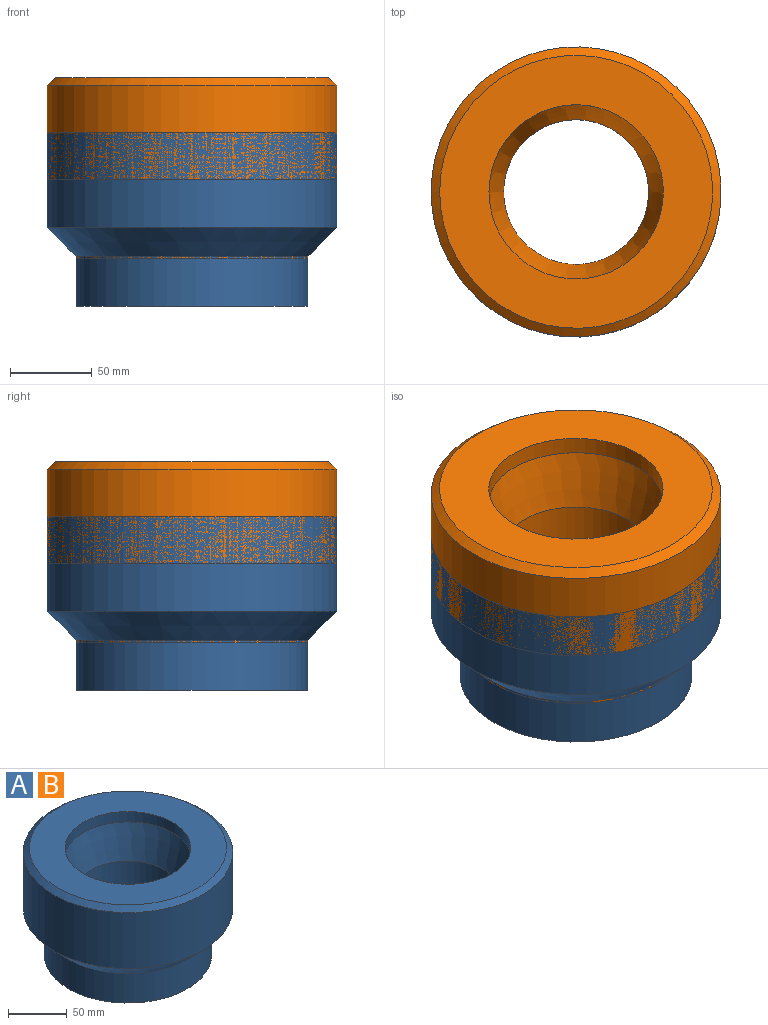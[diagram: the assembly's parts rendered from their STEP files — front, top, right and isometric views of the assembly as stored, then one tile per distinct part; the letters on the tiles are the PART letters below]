
ASSEMBLY  parts=2 mates=1
PART A: 9 faces, bbox 177.8x177.8x110.9 mm
  f0: cylinder r=44.45mm len=88.9mm, axis (0,0,-1), area 18357.3mm2, adj f1,f8
  f1: plane 142.24x142.24mm, normal (0,0,-1), area 9684mm2, adj f0,f2
  f2: cylinder r=71.12mm len=142.24mm, axis (0,0,-1), area 13648.5mm2, adj f1,f3
  f3: cone r=71.12mm half-angle=45deg, axis (0,0,1), area 12639.6mm2, adj f2,f4
  f4: cylinder r=88.9mm len=177.8mm, axis (0,0,-1), area 32466.3mm2, adj f3,f5
  f5: cone r=88.9mm half-angle=49.8deg, axis (0,0,-1), area 3726.1mm2, adj f4,f6
  f6: plane 167.31x167.31mm, normal (0,0,1), area 13013mm2, adj f5,f7
  f7: cylinder r=53.44mm len=106.88mm, axis (0,0,-1), area 3606.3mm2, adj f6,f8
  f8: cone r=53.44mm half-angle=14.6deg, axis (0,0,1), area 10938.2mm2, adj f0,f7
PART B: same geometry as A
PLACE A t=(60.75,-32.2,-45.73)mm
PLACE B t=(60.75,-32.2,-16.67)mm
MATE revolute B.f0 <-> A.f0  axis (0,0,-1) through (60.75,-32.2,31.65)mm
